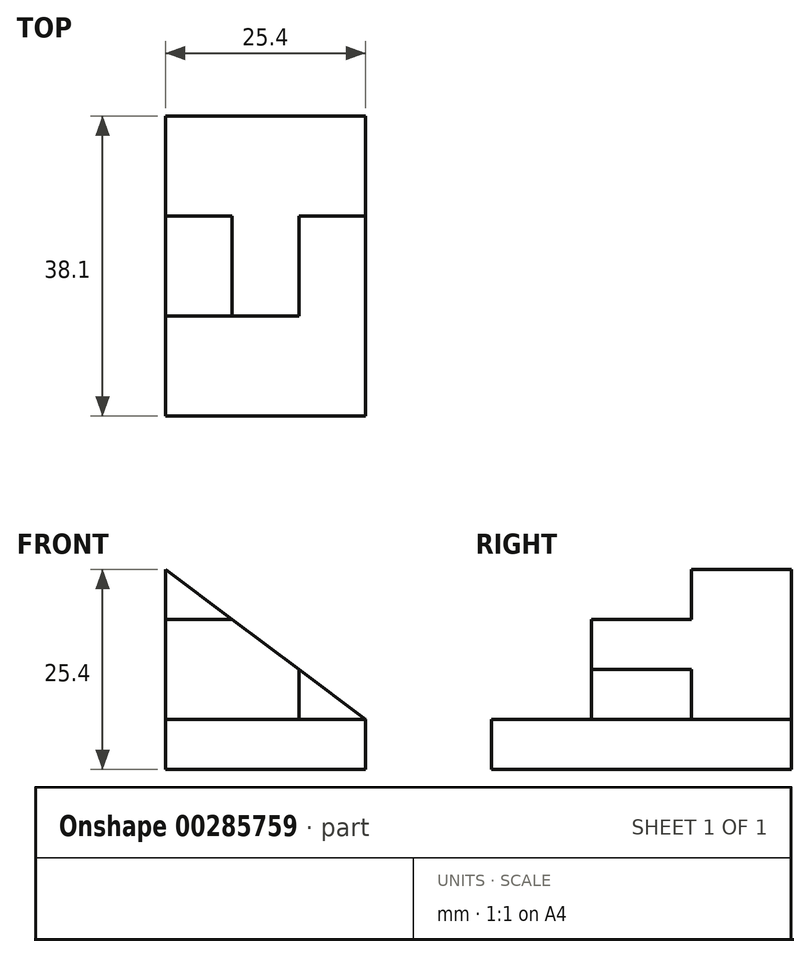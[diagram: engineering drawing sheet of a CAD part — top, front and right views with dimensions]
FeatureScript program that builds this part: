
annotation { "Feature Type Name" : "Feature", "Feature Type Description" : "" }
export const myFeature = defineFeature(function(context is Context, id is Id, definition is map)
    precondition{}
    {
        {
            var Q0;
            Q0=qCreatedBy(makeId("Front.planeOp"),FACE);
            var sketch = newSketch(context, id + "F0", { "sketchPlane" : qUnion([Q0])});
            skLineSegment(sketch, "E0.bottom", {"start": v(0, 0) * mm, "end": v(25.4, 0) * mm});
            skLineSegment(sketch, "E0.top", {"start": v(0, 6.35) * mm, "end": v(25.4, 6.35) * mm});
            skLineSegment(sketch, "E0.left", {"start": v(0, 0) * mm, "end": v(0, 6.35) * mm});
            skLineSegment(sketch, "E0.right", {"start": v(25.4, 0) * mm, "end": v(25.4, 6.35) * mm});
            skSolve(sketch);
        }
        {
            var Q0;
            Q0 = qSketchRegion(id + "F0", true);
            extrude(context, id + "F1", {"entities" : qUnion([Q0]), "depth" : 12.7 * mm});
        }
        {
            var Q0;
            Q0=makeQuery(id+"F1.opExtrude","CAP_FACE",FACE,{"disambiguationData":[OSD([sQuery(id+"F0.wireOp",EDGE,"E0.bottom"),sQuery(id+"F0.wireOp",EDGE,"E0.top"),sQuery(id+"F0.wireOp",EDGE,"E0.left"),sQuery(id+"F0.wireOp",EDGE,"E0.right")])],"isStart":true});
            var sketch = newSketch(context, id + "F2", { "sketchPlane" : qUnion([Q0])});
            skLineSegment(sketch, "E1.bottom", {"start": v(-25.4, 0) * mm, "end": v(0, 0) * mm});
            skLineSegment(sketch, "E1.top", {"start": v(-25.4, 6.35) * mm, "end": v(0, 6.35) * mm});
            skLineSegment(sketch, "E1.left", {"start": v(-25.4, 0) * mm, "end": v(-25.4, 6.35) * mm});
            skLineSegment(sketch, "E1.right", {"start": v(0, 0) * mm, "end": v(0, 6.35) * mm});
            skLineSegment(sketch, "E2", {"start": v(0, 6.35) * mm, "end": v(0, 19.05) * mm});
            skLineSegment(sketch, "E3", {"start": v(0, 19.05) * mm, "end": v(-8.47, 19.05) * mm});
            skLineSegment(sketch, "E4", {"start": v(-8.47, 19.05) * mm, "end": v(-16.93, 12.7) * mm});
            skLineSegment(sketch, "E5", {"start": v(-16.93, 12.7) * mm, "end": v(-16.93, 6.35) * mm});
            skSolve(sketch);
        }
        {
            var Q0;
            Q0 = qSketchRegion(id + "F2", true);
            extrude(context, id + "F3", {"entities" : qUnion([Q0]), "operationType" : NewBodyOperationType.ADD, "depth" : 12.7 * mm});
        }
        {
            var Q0;
            Q0=makeQuery(id+"F3.opExtrude","CAP_FACE",FACE,{"disambiguationData":[OSD([sQuery(id+"F2.wireOp",EDGE,"E1.bottom"),sQuery(id+"F2.wireOp",EDGE,"E1.top"),sQuery(id+"F2.wireOp",EDGE,"E1.left"),sQuery(id+"F2.wireOp",EDGE,"E1.right"),sQuery(id+"F2.wireOp",EDGE,"E2"),sQuery(id+"F2.wireOp",EDGE,"E3"),sQuery(id+"F2.wireOp",EDGE,"E4"),sQuery(id+"F2.wireOp",EDGE,"E5")])],"isStart":false});
            var sketch = newSketch(context, id + "F4", { "sketchPlane" : qUnion([Q0])});
            skLineSegment(sketch, "E6", {"start": v(0, 0) * mm, "end": v(0, 25.4) * mm});
            skPoint(sketch, "E6.endSnap0", {"position": v(0, 9.52) * mm});
            skLineSegment(sketch, "E7", {"start": v(0, 25.4) * mm, "end": v(-25.4, 6.35) * mm});
            skLineSegment(sketch, "E8", {"start": v(-25.4, 6.35) * mm, "end": v(-25.4, 0) * mm});
            skLineSegment(sketch, "E9", {"start": v(-25.4, 0) * mm, "end": v(0, 0) * mm});
            skSolve(sketch);
        }
        {
            var Q0;
            Q0 = qSketchRegion(id + "F4", true);
            extrude(context, id + "F5", {"entities" : qUnion([Q0]), "operationType" : NewBodyOperationType.ADD, "depth" : 12.7 * mm});
        }
    });
